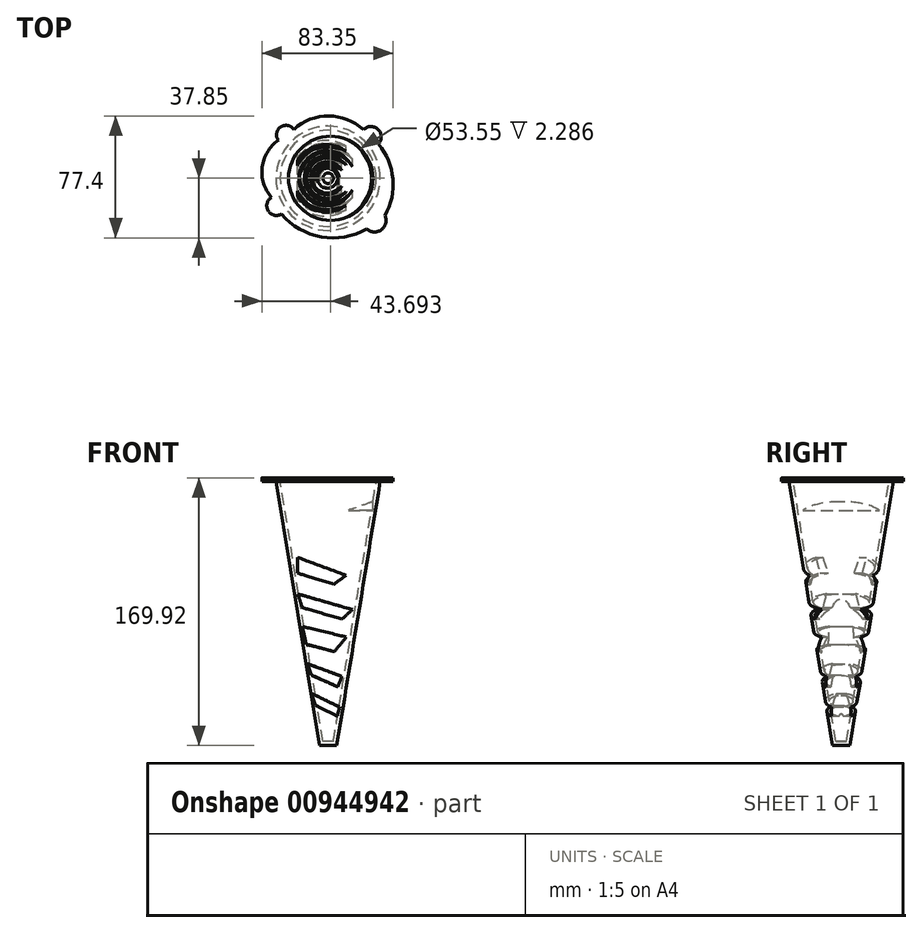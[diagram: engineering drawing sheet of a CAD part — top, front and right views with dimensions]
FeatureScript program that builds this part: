
annotation { "Feature Type Name" : "Feature", "Feature Type Description" : "" }
export const myFeature = defineFeature(function(context is Context, id is Id, definition is map)
    precondition{}
    {
        {
            var Q0;
            Q0=qCreatedBy(makeId("Top.planeOp"),FACE);
            cPlane(context, id + "F0", {"entities" : qUnion([Q0]), "cplaneType" : CPlaneType.OFFSET, "offset" : 87.38 * mm, "width" : 152.4 * mm, "height" : 152.4 * mm});
        }
        {
            var Q0;
            Q0=qCreatedBy(id+"F0.planeOp",FACE);
            cPlane(context, id + "F1", {"entities" : qUnion([Q0]), "cplaneType" : CPlaneType.OFFSET, "offset" : 167.64 * mm, "oppositeDirection" : true, "width" : 152.4 * mm, "height" : 152.4 * mm});
        }
        {
            var Q0;
            Q0=qCreatedBy(id+"F0.planeOp",FACE);
            var sketch = newSketch(context, id + "F2", { "sketchPlane" : qUnion([Q0])});
            skCircle(sketch, "E0", {"center": v(0, 0) * mm, "radius": 33.08 * mm});
            skSolve(sketch);
        }
        {
            var Q0;
            Q0=qCreatedBy(id+"F1.planeOp",FACE);
            var sketch = newSketch(context, id + "F3", { "sketchPlane" : qUnion([Q0])});
            skCircle(sketch, "E1", {"center": v(0, 0) * mm, "radius": 5.46 * mm});
            skSolve(sketch);
        }
        {
            var Q0;
            Q0=makeQuery(id+"F2.imprint","IMPRINT",FACE,{"disambiguationData":[TD([[makeQuery(id+"F2.imprint","IMPRINT",EDGE,{"derivedFrom":sQuery(id+"F2.wireOp",EDGE,"E0")}),1.0]])]});
            var Q1;
            Q1=makeQuery(id+"F3.imprint","IMPRINT",FACE,{"disambiguationData":[TD([[makeQuery(id+"F3.imprint","IMPRINT",EDGE,{"derivedFrom":sQuery(id+"F3.wireOp",EDGE,"E1")}),1.0]])]});
            loft(context, id + "F4", {"sheetProfilesArray" : [{ "sheetProfileEntities" : qUnion([Q0]) }, { "sheetProfileEntities" : qUnion([Q1]) }]});
        }
        {
            var Q0;
            Q0=makeQuery(id+"F4.opLoft","CAP_FACE",FACE,{"disambiguationData":[OSD([makeQuery(id+"F2.imprint","IMPRINT",FACE,{"disambiguationData":[TD([[makeQuery(id+"F2.imprint","IMPRINT",EDGE,{"derivedFrom":sQuery(id+"F2.wireOp",EDGE,"E0")}),1.0]])]})])],"isStart":true});
            shell(context, id + "F5", {"entities" : qUnion([Q0]), "thickness" : 2.54 * mm});
        }
        {
            var Q0;
            Q0=qCreatedBy(makeId("Front.planeOp"),FACE);
            cPlane(context, id + "F6", {"entities" : qUnion([Q0]), "cplaneType" : CPlaneType.OFFSET, "offset" : 33.27 * mm, "oppositeDirection" : true, "width" : 152.4 * mm, "height" : 152.4 * mm});
        }
        {
            var Q0;
            Q0=qCreatedBy(id+"F6.planeOp",FACE);
            var sketch = newSketch(context, id + "F7", { "sketchPlane" : qUnion([Q0])});
            skLineSegment(sketch, "E2", {"start": v(-10.54, -47.18) * mm, "end": v(-7.96, -54.79) * mm});
            skLineSegment(sketch, "E3", {"start": v(-7.96, -54.79) * mm, "end": v(5.83, -61.62) * mm});
            skLineSegment(sketch, "E4", {"start": v(5.83, -61.62) * mm, "end": v(7.25, -55.82) * mm});
            skLineSegment(sketch, "E5", {"start": v(7.25, -55.82) * mm, "end": v(-10.54, -47.18) * mm});
            skLineSegment(sketch, "E6", {"start": v(-10.54, -35.58) * mm, "end": v(-12.99, -28.37) * mm});
            skLineSegment(sketch, "E7", {"start": v(-12.99, -28.37) * mm, "end": v(8.66, -36.36) * mm});
            skLineSegment(sketch, "E8", {"start": v(8.66, -36.36) * mm, "end": v(6.2, -43.01) * mm});
            skLineSegment(sketch, "E9", {"start": v(6.2, -43.01) * mm, "end": v(-10.54, -35.58) * mm});
            skLineSegment(sketch, "E10", {"start": v(-13.9, -16) * mm, "end": v(-16.34, -4.65) * mm});
            skLineSegment(sketch, "E11", {"start": v(-16.34, -4.65) * mm, "end": v(11.5, -11.35) * mm});
            skLineSegment(sketch, "E12", {"start": v(11.5, -11.35) * mm, "end": v(4.02, -20.63) * mm});
            skLineSegment(sketch, "E13", {"start": v(4.02, -20.63) * mm, "end": v(-13.9, -16) * mm});
            skLineSegment(sketch, "E14", {"start": v(-16.34, 7.33) * mm, "end": v(-19.28, 16) * mm});
            skLineSegment(sketch, "E15", {"start": v(-19.28, 16) * mm, "end": v(15.4, 6.03) * mm});
            skLineSegment(sketch, "E16", {"start": v(15.4, 6.03) * mm, "end": v(8.66, 0) * mm});
            skLineSegment(sketch, "E17", {"start": v(8.66, 0) * mm, "end": v(-16.34, 7.33) * mm});
            skLineSegment(sketch, "E18", {"start": v(-19.28, 29.2) * mm, "end": v(-19.28, 39.17) * mm});
            skLineSegment(sketch, "E19", {"start": v(-19.28, 39.17) * mm, "end": v(11.5, 27.81) * mm});
            skLineSegment(sketch, "E20", {"start": v(11.5, 27.81) * mm, "end": v(3.55, 22.19) * mm});
            skLineSegment(sketch, "E21", {"start": v(3.55, 22.19) * mm, "end": v(-19.28, 29.2) * mm});
            skSolve(sketch);
        }
        {
            var Q0;
            Q0 = qSketchRegion(id + "F7", true);
            extrude(context, id + "F8", {"entities" : qUnion([Q0]), "operationType" : NewBodyOperationType.REMOVE, "depth" : 90.42 * mm, "offsetDistance" : 25.4 * mm});
        }
        {
            var Q0;
            Q0=qCreatedBy(id+"F0.planeOp",FACE);
            var sketch = newSketch(context, id + "F9", { "sketchPlane" : qUnion([Q0])});
            skArc(sketch, "E22", {"start": v(-29.66, -22.76) * mm, "mid": v(-4.26, -37.2) * mm, "end": v(24.54, -32.22) * mm});
            skArc(sketch, "E23", {"start": v(24.54, -32.22) * mm, "mid": v(33.8, -32.7) * mm, "end": v(36.16, -23.75) * mm});
            skArc(sketch, "E24", {"start": v(36.16, -23.75) * mm, "mid": v(41.11, -0.35) * mm, "end": v(32.02, 21.78) * mm});
            skArc(sketch, "E25", {"start": v(32.02, 21.78) * mm, "mid": v(31.66, 31.07) * mm, "end": v(22.37, 30.84) * mm});
            skArc(sketch, "E26", {"start": v(22.37, 30.84) * mm, "mid": v(0.34, 39.55) * mm, "end": v(-21.78, 31.07) * mm});
            skPoint(sketch, "E26.endSnap0", {"position": v(31.66, 31.07) * mm});
            skArc(sketch, "E27", {"start": v(-21.78, 31.07) * mm, "mid": v(-30.19, 32.57) * mm, "end": v(-31.63, 24.14) * mm});
            skArc(sketch, "E28", {"start": v(-31.63, 24.14) * mm, "mid": v(-41.9, 6.98) * mm, "end": v(-35.97, -12.12) * mm});
            skArc(sketch, "E29", {"start": v(-35.97, -12.12) * mm, "mid": v(-38.1, -20.57) * mm, "end": v(-29.66, -22.76) * mm});
            skSolve(sketch);
        }
        {
            var Q0;
            Q0 = qSketchRegion(id + "F9", true);
            extrude(context, id + "F10", {"entities" : qUnion([Q0]), "operationType" : NewBodyOperationType.ADD, "depth" : 2.3 * mm, "offsetDistance" : 25.4 * mm});
        }
        {
            var Q0;
            Q0=makeQuery(id+"F10.opExtrude","CAP_FACE",FACE,{"disambiguationData":[OSD([sQuery(id+"F9.wireOp",EDGE,"E22"),sQuery(id+"F9.wireOp",EDGE,"E23"),sQuery(id+"F9.wireOp",EDGE,"E24"),sQuery(id+"F9.wireOp",EDGE,"E25"),sQuery(id+"F9.wireOp",EDGE,"E26"),sQuery(id+"F9.wireOp",EDGE,"E27"),sQuery(id+"F9.wireOp",EDGE,"E28"),sQuery(id+"F9.wireOp",EDGE,"E29")])],"isStart":false});
            var sketch = newSketch(context, id + "F11", { "sketchPlane" : qUnion([Q0])});
            skCircle(sketch, "E30", {"center": v(1.62, 0) * mm, "radius": 26.78 * mm});
            skSolve(sketch);
        }
        {
            var Q0;
            Q0=makeQuery(id+"F11.imprint","IMPRINT",FACE,{"disambiguationData":[TD([[makeQuery(id+"F11.imprint","IMPRINT",EDGE,{"derivedFrom":sQuery(id+"F11.wireOp",EDGE,"E30")}),1.0]])]});
            extrude(context, id + "F12", {"entities" : qUnion([Q0]), "operationType" : NewBodyOperationType.REMOVE, "oppositeDirection" : true, "depth" : 20.57 * mm, "offsetDistance" : 25.4 * mm});
        }
    });
